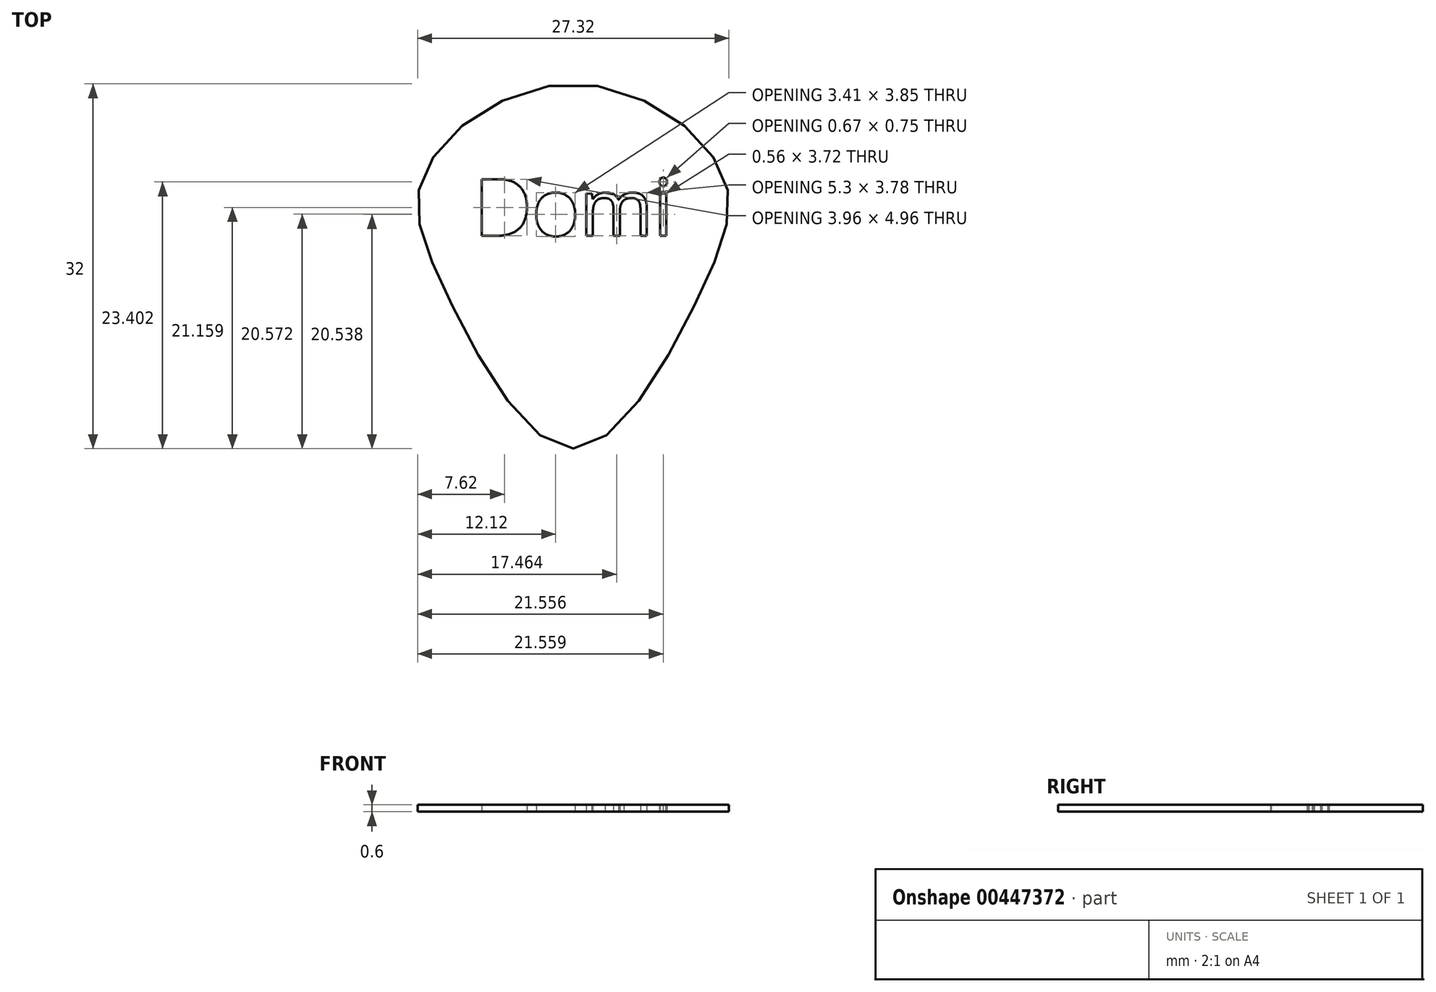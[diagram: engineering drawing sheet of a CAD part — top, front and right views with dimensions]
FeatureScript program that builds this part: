
annotation { "Feature Type Name" : "Feature", "Feature Type Description" : "" }
export const myFeature = defineFeature(function(context is Context, id is Id, definition is map)
    precondition{}
    {
        {
            var Q0;
            Q0=qCreatedBy(makeId("Top.planeOp"),FACE);
            var sketch = newSketch(context, id + "F0", { "sketchPlane" : qUnion([Q0])});
            skPoint(sketch, "E0", {"position": v(-13, 11) * mm});
            skPoint(sketch, "E1", {"position": v(13, 11) * mm});
            skPoint(sketch, "E2", {"position": v(0, -13.35) * mm});
            skPoint(sketch, "E3", {"position": v(0, 18.65) * mm});
            skPoint(sketch, "E4", {"position": v(-11, 0) * mm});
            skPoint(sketch, "E5", {"position": v(11, 0) * mm});
            skFitSpline(sketch, "E6", {"points": [v(0, -13.35) * mm, v(-11, 0) * mm, v(-13, 11) * mm, v(0, 18.65) * mm, v(13, 11) * mm, v(11, 0) * mm, v(0, -13.35) * mm]});
            skText(sketch, "E7", { "text": "Domi", "fontName": "OpenSans-Regular.ttf"});
            const initialGuessF0  = {"E7": [-0.0087, 0.00533, 1, 0, 0.005]};
            skSetInitialGuess(sketch, initialGuessF0);
            skSolve(sketch);
        }
        {
            var Q0;
            Q0=makeQuery(id+"F0.imprint","IMPRINT",FACE,{"disambiguationData":[TD([[makeQuery(id+"F0.imprint","IMPRINT",EDGE,{"derivedFrom":sQuery(id+"F0.wireOp",EDGE,"E6")}),-1.0]])]});
            extrude(context, id + "F1", {"entities" : qUnion([Q0]), "depth" : 0.6 * mm});
        }
    });
